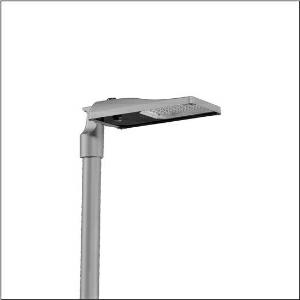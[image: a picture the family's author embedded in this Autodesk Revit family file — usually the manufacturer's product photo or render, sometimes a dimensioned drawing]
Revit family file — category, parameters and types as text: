
# Revit family: streetlight_sl_31_mini___st0_8a_5xh6c31t08ha_0974
name_source: partatom
category: Lighting Fixtures
units: mm (PartAtom-declared; Revit-internal decimal feet)

## family parameters
Cut with Voids When Loaded = No
Host = Face
Light Source = No
Part Type = Normal
Room Calculation Point = No
Round Connector Dimension = Use Diameter
Shared = No

## types (1)
- --- (1 x LED, 9230 lm, 68.3 W, 3000K)
    Apparent Load = 68 VA
    CIE Flux Codes = 38 75 97 100 100
    Color Rendering = 70
    Color Temperature = 3000K
    Default Elevation = 1800 mm
    Description = Streetlight SL 31 mini D4i, Desk-Remote mast luminaire for post-top, side-entry; light control with lens of PMMA; light distribution: ST0.8a, direct asymmetric distribution, for standard-compliant lighting for roads and squares; LED: luminous flux: 9.230lm, light colour: 730, colour temperature: 3000K; luminous efficacy: 135,1lm/W; control: pre-setting: logarithmic dimming characteristic, flexible luminous flux parameterisation, time-dependent luminous flux control, constant luminous flux control, power reduction, intelligent temperature release in ECG and LED module, overheat protection; luminaire housing, of diecast aluminium, Siteco® metallic grey (DB 702S), corrosivity category C5 high according to DIN EN ISO 12944; cover of toughened safety glass, transparent, opened without tools; mast flange of diecast aluminium, Siteco® metallic grey (DB 702S), spigot size: 76/60mm, mast flange included unmounted; with cable H07RN-F 2x 1.5mm², cable length: 8,5m, connection cable pre-assembled; mains connection: 220..240V, AC, 50/60Hz; power consumption (at start of service life): 68,3W / (at end of service life): 74,5W / (with reduced operation 50%): 29,5W; protection rating (complete): IP66; insulation class (complete): insulation class II (safety insulation); impact resistance: IK09; certification: CE, ENEC, ENEC+, VDE, UKCA, ZD4i; permissible operating ambient temperature for outdoor applications: -40..+50°C; packaging unit: 1 piece

Light Distribution: ST0.8a
    Height = 76 mm
    Lamp = 1 x LED
    Lamp Light Flux = 9230 lm
    Lamp Power = 68.3 W
    Lamp count = 1
    Length = 547 mm
    Luminous efficacy = 135 lm/W
    Manufacturer = Siteco
    ModVariant = No
    Model = 5XH6C31T08HA
    Number of Poles = 1
    OnlyDefault = Yes
    Power Factor = 1
    Product Name = Streetlight SL 31 mini | ST0.8a
    Product group = mast luminaire | pylon top
    ProductGroupID = 6100
    Protection Class = Protection class II
    Protection Degree = IP 66
    RLX_Detail_Level = 1
    RLX_Emergency_Light_Flux = 0 lm
    RLX_Emergency_Type = 0
    RLX_Emergency_Type_DB = No
    RlxData = <blob elided: 24417 chars, md5=0a9e0ae3>
    Socket = socket
    Standby Power = 0 W
    System Light Flux = 9230 lm
    System Power = 68 W
    Type Comments = factory setting: luminous flux: 100 % | dim-lin: 254 | 692 mA
    Type Image = l_1300332.jpg
    URL = http://relux.com
    VarID = @adj_001679
    Voltage = 0 V
    Weight = 0.00 kg
    Width = 265 mm

## geometry (parser evidence)
native form markers: Blend x4, Sweep x9
no freeform markers — native parametric forms only
